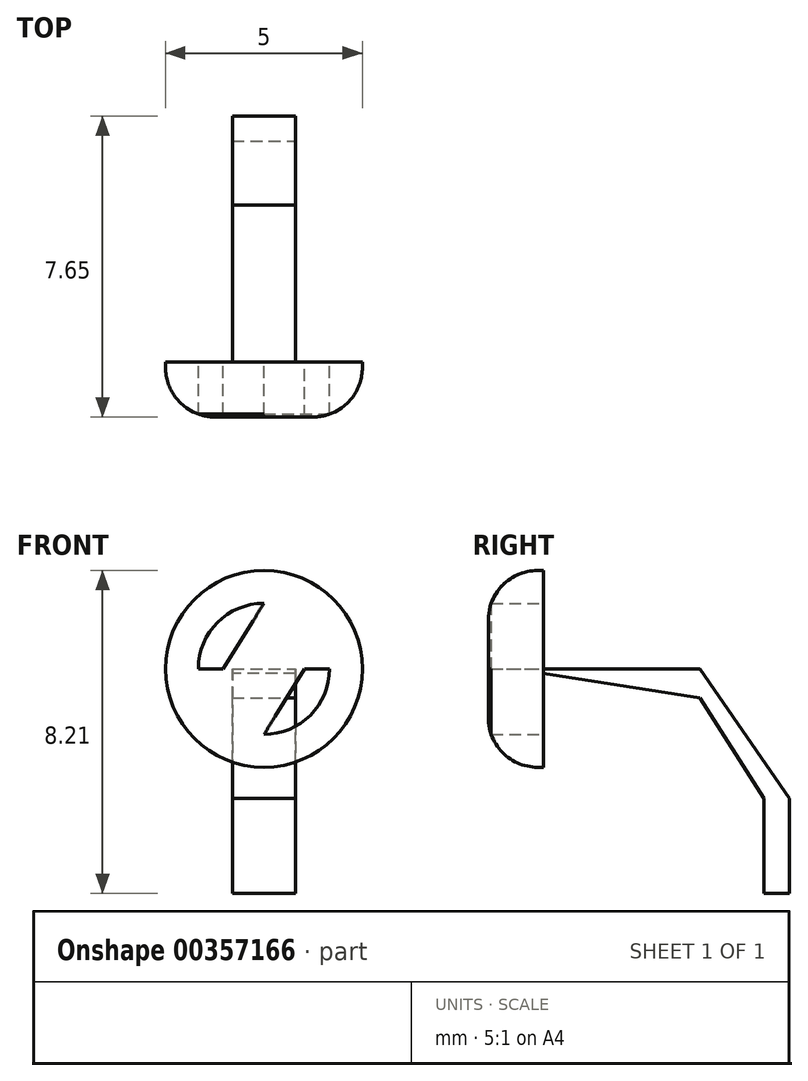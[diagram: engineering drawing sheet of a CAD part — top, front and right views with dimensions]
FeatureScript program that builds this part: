
annotation { "Feature Type Name" : "Feature", "Feature Type Description" : "" }
export const myFeature = defineFeature(function(context is Context, id is Id, definition is map)
    precondition{}
    {
        {
            var Q0;
            Q0=qCreatedBy(makeId("Front.planeOp"),FACE);
            var sketch = newSketch(context, id + "F0", { "sketchPlane" : qUnion([Q0])});
            skCircle(sketch, "E0", {"center": v(0, 0) * mm, "radius": 1.67 * mm});
            skCircle(sketch, "E1", {"center": v(0, 0) * mm, "radius": 2.5 * mm});
            skLineSegment(sketch, "E2", {"start": v(0, 1.67) * mm, "end": v(-1.04, 0) * mm});
            skLineSegment(sketch, "E3", {"start": v(-1.04, 0) * mm, "end": v(0, -1.67) * mm});
            skLineSegment(sketch, "E4.MirrorCS", {"start": v(0, 1.67) * mm, "end": v(1.04, 0) * mm});
            skLineSegment(sketch, "E5.MirrorCS", {"start": v(1.04, 0) * mm, "end": v(0, -1.67) * mm});
            skLineSegment(sketch, "E6", {"start": v(-1.04, 0) * mm, "end": v(-1.67, 0) * mm});
            skLineSegment(sketch, "E7", {"start": v(1.04, 0) * mm, "end": v(1.67, 0) * mm});
            skSolve(sketch);
        }
        {
            var Q0;
            Q0=qCreatedBy(makeId("Right.planeOp"),FACE);
            var sketch = newSketch(context, id + "F1", { "sketchPlane" : qUnion([Q0])});
            skLineSegment(sketch, "E8", {"start": v(0, 0) * mm, "end": v(4.68, 0) * mm});
            skLineSegment(sketch, "E9", {"start": v(4.68, 0) * mm, "end": v(6.95, -3.3) * mm});
            skLineSegment(sketch, "E10", {"start": v(6.95, -3.3) * mm, "end": v(6.95, -4.32) * mm});
            skLineSegment(sketch, "E11", {"start": v(6.95, -4.32) * mm, "end": v(6.95, -5.7) * mm});
            skLineSegment(sketch, "E12", {"start": v(6.95, -5.7) * mm, "end": v(6.3, -5.7) * mm});
            skLineSegment(sketch, "E13", {"start": v(6.3, -5.7) * mm, "end": v(6.3, -4.32) * mm});
            skLineSegment(sketch, "E14", {"start": v(6.3, -4.32) * mm, "end": v(6.3, -3.3) * mm});
            skLineSegment(sketch, "E15", {"start": v(6.3, -3.3) * mm, "end": v(4.68, -0.74) * mm});
            skLineSegment(sketch, "E16", {"start": v(4.68, -0.74) * mm, "end": v(0, 0) * mm});
            skSolve(sketch);
        }
        {
            var Q0;
            Q0 = qSketchRegion(id + "F0", true);
            var Q1;
            Q1=makeQuery(id+"F0.imprint","IMPRINT",FACE,{"disambiguationData":[TD([[makeQuery(id+"F0.imprint","IMPRINT",EDGE,{"derivedFrom":sQuery(id+"F0.wireOp",EDGE,"E2")}),1.0]])]});
            var Q2;
            {var subQ0=sQuery(id+"F0.wireOp",EDGE,"E4.MirrorCS");Q2=makeQuery(id+"F0.imprint","IMPRINT",FACE,{"disambiguationData":[TD([[makeQuery(id+"F0.imprint","IMPRINT",EDGE,{"derivedFrom":subQ0}),1.0]])]});}
            var Q3;
            {var subQ0=sQuery(id+"F0.wireOp",EDGE,"E3");Q3=makeQuery(id+"F0.imprint","IMPRINT",FACE,{"disambiguationData":[TD([[makeQuery(id+"F0.imprint","IMPRINT",EDGE,{"derivedFrom":subQ0}),-1.0]])]});}
            extrude(context, id + "F2", {"entities" : qUnion([Q0, Q1, Q2, Q3]), "endBound" : BoundingType.SYMMETRIC, "depth" : 1.4 * mm});
        }
        {
            var Q0;
            Q0=makeQuery(id+"F1.imprint","IMPRINT",FACE,{"disambiguationData":[TD([[makeQuery(id+"F1.imprint","IMPRINT",EDGE,{"derivedFrom":sQuery(id+"F1.wireOp",EDGE,"E8")}),-1.0]])]});
            extrude(context, id + "F3", {"entities" : qUnion([Q0]), "operationType" : NewBodyOperationType.ADD, "endBound" : BoundingType.SYMMETRIC, "oppositeDirection" : true, "depth" : 1.6 * mm});
        }
        {
            var Q0;
            Q0=makeQuery(id+"F2.opExtrude","CAP_EDGE",EDGE,{"disambiguationData":[OSD([sQuery(id+"F0.wireOp",EDGE,"E1")])],"isStart":false});
            fillet(context, id + "F4", {"entities" : qUnion([Q0]), "radius" : 1.26 * mm, "tangentPropagation" : true, "allowEdgeOverflow" : false});
        }
    });
